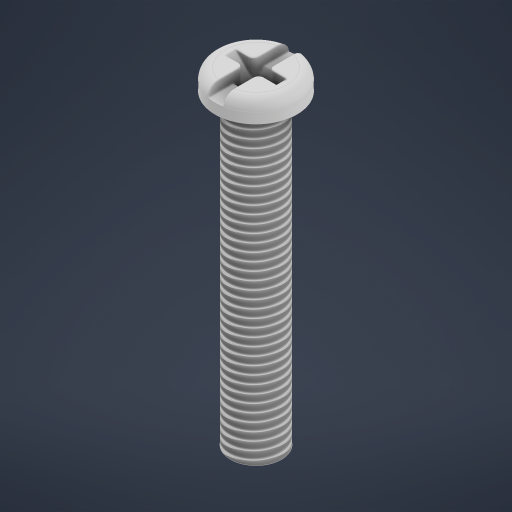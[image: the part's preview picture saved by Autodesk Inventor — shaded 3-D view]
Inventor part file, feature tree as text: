
AUTODESK INVENTOR PART (.ipt)
format: ipt  version: 2023.2 (Build 272271000, 271)  size: 343,552 bytes
history: native  units: mm
features: sketch x1, thread x1
ambient origin geometry x8: Origin, YZ Plane, XZ Plane, XY Plane, X Axis, Y Axis, Z Axis, Center Point
bodies: Body1 (feature_tree)
feature tree (2):
  sketch  "Sketch1"  dims[d229=8.0mm d230=30.0mm d231=0.0mm d232=2.0mm d233=0.0mm d234=8.0mm d235=1.5mm d236=1.0mm d237=5.0mm d238=5.0mm d239=1.0mm d240=0.0mm d243=1.0mm d244=1.0mm d245=2.0mm d246=0.0mm d247=2.0mm d248=2.0mm d249=45.0deg d257=2.0mm d258=0.0mm d259=30.0mm d260=0.0mm d264=0.5mm d265=1.0mm d266=0.5mm d9=0.5mm d10=0.872665mm d11=0.5mm d12=0.872665mm d13=0.5mm d14=0.872665mm d27=0.5mm d28=0.872665mm d29=0.5mm d30=0.872665mm d88=0.5mm d89=0.872665mm d90=0.5mm d91=0.872665mm d116=0.5mm d117=0.872665mm d118=0.5mm d119=0.872665mm d154=0.5mm d155=0.872665mm d156=0.5mm d157=0.872665mm d181=0.5mm d182=0.872665mm d183=0.5mm d184=0.872665mm d221=0.5mm d222=0.872665mm d223=0.5mm d224=0.872665mm d267=0.0mm d268=0.0mm d269=0.0mm d270=0.0mm]
  thread  "Thread1"  [1 undecoded]
note: 1 required parameter value undecoded (feature->parameter linkage not recoverable at this tier; creation-order binding heuristic only, values carry confidence <= 0.55)
